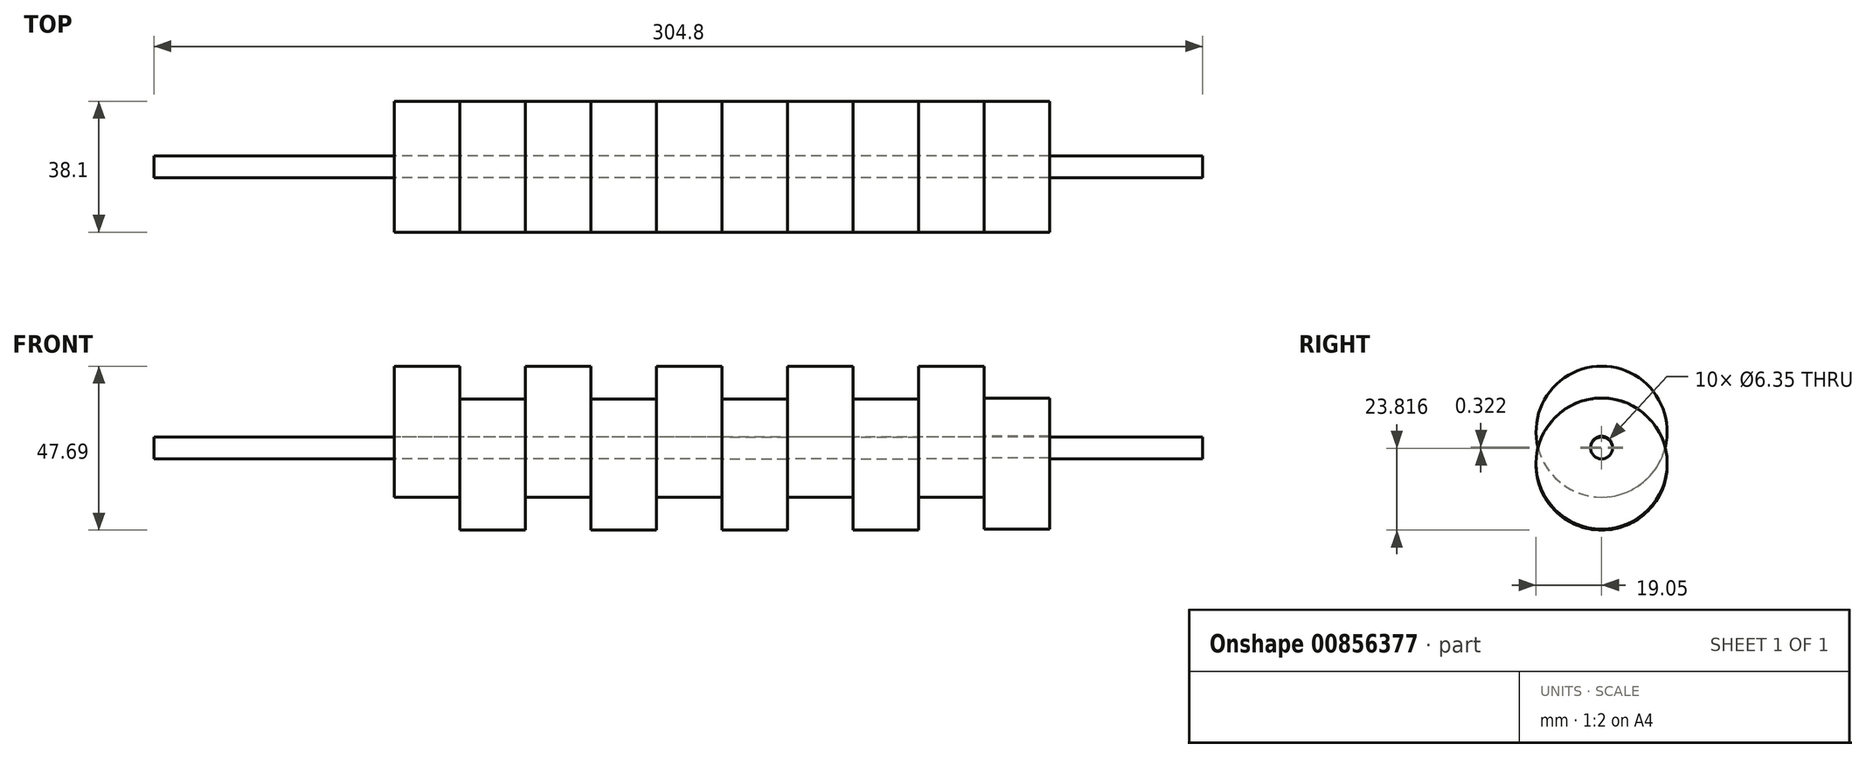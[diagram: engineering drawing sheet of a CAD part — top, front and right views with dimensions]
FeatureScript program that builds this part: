
annotation { "Feature Type Name" : "Feature", "Feature Type Description" : "" }
export const myFeature = defineFeature(function(context is Context, id is Id, definition is map)
    precondition{}
    {
        {
            var Q0;
            Q0=qCreatedBy(makeId("Right.planeOp"),FACE);
            cPlane(context, id + "F0", {"entities" : qUnion([Q0]), "cplaneType" : CPlaneType.OFFSET, "offset" : 50.8 * mm, "width" : 152.4 * mm, "height" : 152.4 * mm});
        }
        {
            var Q0;
            Q0=qCreatedBy(id+"F0.planeOp",FACE);
            var sketch = newSketch(context, id + "F1", { "sketchPlane" : qUnion([Q0])});
            skCircle(sketch, "E0", {"center": v(0, 0) * mm, "radius": 3.18 * mm});
            skCircle(sketch, "E1", {"center": v(0, 4.76) * mm, "radius": 19.05 * mm});
            skPoint(sketch, "E1.first.point", {"position": v(0, 23.81) * mm});
            skPoint(sketch, "E1.second.point", {"position": v(0, -14.29) * mm});
            skPoint(sketch, "E1.third.point", {"position": v(-9.1, -11.97) * mm});
            skSolve(sketch);
        }
        {
            var Q0;
            Q0=qCreatedBy(id+"F0.planeOp",FACE);
            cPlane(context, id + "F2", {"entities" : qUnion([Q0]), "cplaneType" : CPlaneType.OFFSET, "offset" : 19.05 * mm, "width" : 152.4 * mm, "height" : 152.4 * mm});
        }
        {
            var Q0;
            Q0=qCreatedBy(id+"F2.planeOp",FACE);
            cPlane(context, id + "F3", {"entities" : qUnion([Q0]), "cplaneType" : CPlaneType.OFFSET, "offset" : 19.05 * mm, "width" : 152.4 * mm, "height" : 152.4 * mm});
        }
        {
            var Q0;
            Q0=qCreatedBy(id+"F3.planeOp",FACE);
            cPlane(context, id + "F4", {"entities" : qUnion([Q0]), "cplaneType" : CPlaneType.OFFSET, "offset" : 19.05 * mm, "width" : 152.4 * mm, "height" : 152.4 * mm});
        }
        {
            var Q0;
            Q0=qCreatedBy(id+"F4.planeOp",FACE);
            cPlane(context, id + "F5", {"entities" : qUnion([Q0]), "cplaneType" : CPlaneType.OFFSET, "offset" : 19.05 * mm, "width" : 152.4 * mm, "height" : 152.4 * mm});
        }
        {
            var Q0;
            Q0=qCreatedBy(id+"F5.planeOp",FACE);
            cPlane(context, id + "F6", {"entities" : qUnion([Q0]), "cplaneType" : CPlaneType.OFFSET, "offset" : 19.05 * mm, "width" : 152.4 * mm, "height" : 152.4 * mm});
        }
        {
            var Q0;
            Q0=qCreatedBy(id+"F6.planeOp",FACE);
            cPlane(context, id + "F7", {"entities" : qUnion([Q0]), "cplaneType" : CPlaneType.OFFSET, "offset" : 19.05 * mm, "width" : 152.4 * mm, "height" : 152.4 * mm});
        }
        {
            var Q0;
            Q0=qCreatedBy(id+"F7.planeOp",FACE);
            cPlane(context, id + "F8", {"entities" : qUnion([Q0]), "cplaneType" : CPlaneType.OFFSET, "offset" : 19.05 * mm, "width" : 152.4 * mm, "height" : 152.4 * mm});
        }
        {
            var Q0;
            Q0=qCreatedBy(id+"F8.planeOp",FACE);
            cPlane(context, id + "F9", {"entities" : qUnion([Q0]), "cplaneType" : CPlaneType.OFFSET, "offset" : 19.05 * mm, "width" : 152.4 * mm, "height" : 152.4 * mm});
        }
        {
            var Q0;
            Q0=qCreatedBy(id+"F9.planeOp",FACE);
            cPlane(context, id + "F10", {"entities" : qUnion([Q0]), "cplaneType" : CPlaneType.OFFSET, "offset" : 19.05 * mm, "width" : 152.4 * mm, "height" : 152.4 * mm});
        }
        {
            var Q0;
            Q0=qCreatedBy(id+"F3.planeOp",FACE);
            var sketch = newSketch(context, id + "F11", { "sketchPlane" : qUnion([Q0])});
            skCircle(sketch, "E2", {"center": v(0, 0) * mm, "radius": 3.18 * mm});
            skCircle(sketch, "E3", {"center": v(0, 4.76) * mm, "radius": 19.05 * mm});
            skSolve(sketch);
        }
        {
            var Q0;
            Q0=qCreatedBy(id+"F5.planeOp",FACE);
            var sketch = newSketch(context, id + "F12", { "sketchPlane" : qUnion([Q0])});
            skCircle(sketch, "E4", {"center": v(0, 0) * mm, "radius": 3.18 * mm});
            skCircle(sketch, "E5", {"center": v(0, 4.76) * mm, "radius": 19.05 * mm});
            skSolve(sketch);
        }
        {
            var Q0;
            Q0=qCreatedBy(id+"F7.planeOp",FACE);
            var sketch = newSketch(context, id + "F13", { "sketchPlane" : qUnion([Q0])});
            skCircle(sketch, "E6", {"center": v(0, 0) * mm, "radius": 3.18 * mm});
            skCircle(sketch, "E7", {"center": v(0, 4.76) * mm, "radius": 19.05 * mm});
            skSolve(sketch);
        }
        {
            var Q0;
            Q0=qCreatedBy(id+"F9.planeOp",FACE);
            var sketch = newSketch(context, id + "F14", { "sketchPlane" : qUnion([Q0])});
            skCircle(sketch, "E8", {"center": v(0, 0) * mm, "radius": 3.18 * mm});
            skCircle(sketch, "E9", {"center": v(0, 4.76) * mm, "radius": 19.05 * mm});
            skSolve(sketch);
        }
        {
            var Q0;
            Q0=qCreatedBy(id+"F2.planeOp",FACE);
            var sketch = newSketch(context, id + "F15", { "sketchPlane" : qUnion([Q0])});
            skCircle(sketch, "E10", {"center": v(0, 0) * mm, "radius": 3.18 * mm});
            skCircle(sketch, "E11", {"center": v(0, -4.76) * mm, "radius": 19.05 * mm});
            skSolve(sketch);
        }
        {
            var Q0;
            Q0=qCreatedBy(id+"F4.planeOp",FACE);
            var sketch = newSketch(context, id + "F16", { "sketchPlane" : qUnion([Q0])});
            skCircle(sketch, "E12", {"center": v(0, -0.01) * mm, "radius": 3.18 * mm});
            skCircle(sketch, "E13", {"center": v(0, -4.78) * mm, "radius": 19.05 * mm});
            skSolve(sketch);
        }
        {
            var Q0;
            Q0=qCreatedBy(id+"F6.planeOp",FACE);
            var sketch = newSketch(context, id + "F17", { "sketchPlane" : qUnion([Q0])});
            skCircle(sketch, "E14", {"center": v(0, -0.06) * mm, "radius": 3.18 * mm});
            skCircle(sketch, "E15", {"center": v(0, -4.83) * mm, "radius": 19.05 * mm});
            skSolve(sketch);
        }
        {
            var Q0;
            Q0=qCreatedBy(id+"F8.planeOp",FACE);
            var sketch = newSketch(context, id + "F18", { "sketchPlane" : qUnion([Q0])});
            skCircle(sketch, "E16", {"center": v(0, -0.06) * mm, "radius": 3.18 * mm});
            skCircle(sketch, "E17", {"center": v(0, -4.83) * mm, "radius": 19.05 * mm});
            skSolve(sketch);
        }
        {
            var Q0;
            Q0=qCreatedBy(id+"F10.planeOp",FACE);
            var sketch = newSketch(context, id + "F19", { "sketchPlane" : qUnion([Q0])});
            skCircle(sketch, "E18", {"center": v(0, 0.26) * mm, "radius": 3.18 * mm});
            skCircle(sketch, "E19", {"center": v(0, -4.5) * mm, "radius": 19.05 * mm});
            skSolve(sketch);
        }
        {
            var Q0;
            Q0=makeQuery(id+"F1.imprint","IMPRINT",FACE,{"disambiguationData":[TD([[makeQuery(id+"F1.imprint","IMPRINT",EDGE,{"derivedFrom":sQuery(id+"F1.wireOp",EDGE,"E0")}),-1.0]])]});
            var Q1;
            Q1=makeQuery(id+"F15.imprint","IMPRINT",FACE,{"disambiguationData":[TD([[makeQuery(id+"F15.imprint","IMPRINT",EDGE,{"derivedFrom":sQuery(id+"F15.wireOp",EDGE,"E10")}),-1.0]])]});
            var Q2;
            Q2=makeQuery(id+"F11.imprint","IMPRINT",FACE,{"disambiguationData":[TD([[makeQuery(id+"F11.imprint","IMPRINT",EDGE,{"derivedFrom":sQuery(id+"F11.wireOp",EDGE,"E2")}),-1.0]])]});
            var Q3;
            Q3=makeQuery(id+"F16.imprint","IMPRINT",FACE,{"disambiguationData":[TD([[makeQuery(id+"F16.imprint","IMPRINT",EDGE,{"derivedFrom":sQuery(id+"F16.wireOp",EDGE,"E12")}),-1.0]])]});
            var Q4;
            Q4=makeQuery(id+"F12.imprint","IMPRINT",FACE,{"disambiguationData":[TD([[makeQuery(id+"F12.imprint","IMPRINT",EDGE,{"derivedFrom":sQuery(id+"F12.wireOp",EDGE,"E4")}),-1.0]])]});
            var Q5;
            Q5=makeQuery(id+"F17.imprint","IMPRINT",FACE,{"disambiguationData":[TD([[makeQuery(id+"F17.imprint","IMPRINT",EDGE,{"derivedFrom":sQuery(id+"F17.wireOp",EDGE,"E14")}),-1.0]])]});
            var Q6;
            Q6=makeQuery(id+"F13.imprint","IMPRINT",FACE,{"disambiguationData":[TD([[makeQuery(id+"F13.imprint","IMPRINT",EDGE,{"derivedFrom":sQuery(id+"F13.wireOp",EDGE,"E6")}),-1.0]])]});
            var Q7;
            Q7=makeQuery(id+"F18.imprint","IMPRINT",FACE,{"disambiguationData":[TD([[makeQuery(id+"F18.imprint","IMPRINT",EDGE,{"derivedFrom":sQuery(id+"F18.wireOp",EDGE,"E16")}),-1.0]])]});
            var Q8;
            Q8=makeQuery(id+"F14.imprint","IMPRINT",FACE,{"disambiguationData":[TD([[makeQuery(id+"F14.imprint","IMPRINT",EDGE,{"derivedFrom":sQuery(id+"F14.wireOp",EDGE,"E8")}),-1.0]])]});
            var Q9;
            Q9=makeQuery(id+"F19.imprint","IMPRINT",FACE,{"disambiguationData":[TD([[makeQuery(id+"F19.imprint","IMPRINT",EDGE,{"derivedFrom":sQuery(id+"F19.wireOp",EDGE,"E18")}),-1.0]])]});
            extrude(context, id + "F20", {"entities" : qUnion([Q0, Q1, Q2, Q3, Q4, Q5, Q6, Q7, Q8, Q9]), "depth" : 19.05 * mm, "offsetDistance" : 25.4 * mm});
        }
        {
            var Q0;
            Q0=qCreatedBy(makeId("Front.planeOp"),FACE);
            var sketch = newSketch(context, id + "F21", { "sketchPlane" : qUnion([Q0])});
            skLineSegment(sketch, "E20.bottom", {"start": v(-19.05, 0) * mm, "end": v(285.75, 0) * mm});
            skLineSegment(sketch, "E20.top", {"start": v(-19.05, 3.17) * mm, "end": v(285.75, 3.17) * mm});
            skLineSegment(sketch, "E20.left", {"start": v(-19.05, 0) * mm, "end": v(-19.05, 3.17) * mm});
            skLineSegment(sketch, "E20.right", {"start": v(285.75, 0) * mm, "end": v(285.75, 3.17) * mm});
            skSolve(sketch);
        }
        {
            var Q0;
            Q0=makeQuery(id+"F21.imprint","IMPRINT",FACE,{"disambiguationData":[TD([[makeQuery(id+"F21.imprint","IMPRINT",EDGE,{"derivedFrom":sQuery(id+"F21.wireOp",EDGE,"E20.bottom")}),1.0]])]});
            var Q1;
            Q1=sQuery(id+"F21.wireOp",EDGE,"E20.bottom");
            revolve(context, id + "F22", {"surfaceOperationType" : NewSurfaceOperationType.NEW, "entities" : qUnion([Q0]), "axis" : qUnion([Q1]), "revolveType" : RevolveType.FULL});
        }
    });
